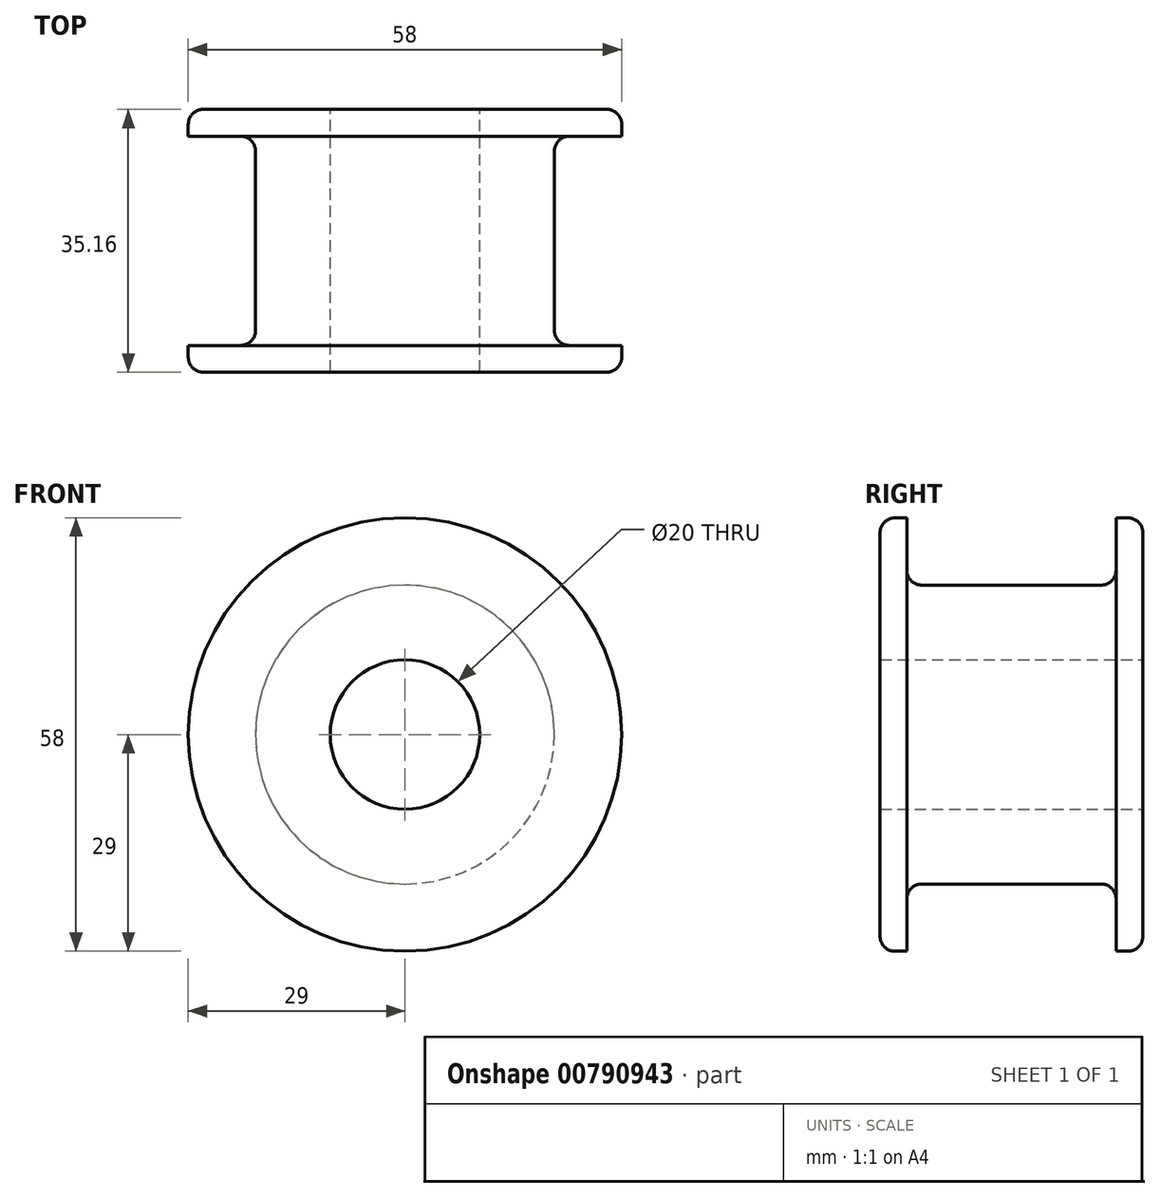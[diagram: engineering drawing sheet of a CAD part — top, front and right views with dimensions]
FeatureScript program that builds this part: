
annotation { "Feature Type Name" : "Feature", "Feature Type Description" : "" }
export const myFeature = defineFeature(function(context is Context, id is Id, definition is map)
    precondition{}
    {
        {
            var Q0;
            Q0=qCreatedBy(makeId("Top.planeOp"),FACE);
            var sketch = newSketch(context, id + "F0", { "sketchPlane" : qUnion([Q0])});
            skLineSegment(sketch, "E0", {"start": v(-29, -14) * mm, "end": v(-29, -17.6) * mm});
            skLineSegment(sketch, "E1", {"start": v(-29, -14) * mm, "end": v(-20, -14) * mm});
            skLineSegment(sketch, "E2", {"start": v(-20, -14) * mm, "end": v(-20, 0) * mm});
            skLineSegment(sketch, "E3", {"start": v(-20, 0) * mm, "end": v(0, 0) * mm});
            skLineSegment(sketch, "E4", {"start": v(0, 0) * mm, "end": v(0, -17.5) * mm});
            skLineSegment(sketch, "E5", {"start": v(-29, -17.6) * mm, "end": v(0, -17.5) * mm});
            skSolve(sketch);
        }
        {
            var Q0;
            Q0 = qSketchRegion(id + "F0", true);
            var Q1;
            Q1=sQuery(id+"F0.wireOp",EDGE,"E4");
            revolve(context, id + "F1", {"surfaceOperationType" : NewSurfaceOperationType.NEW, "entities" : qUnion([Q0]), "axis" : qUnion([Q1]), "revolveType" : RevolveType.FULL});
        }
        {
            var Q0;
            Q0=makeQuery(id+"F1.opRevolve","SWEPT_BODY",BODY,{"disambiguationData":[OSD([sQuery(id+"F0.wireOp",EDGE,"E0"),sQuery(id+"F0.wireOp",EDGE,"E1"),sQuery(id+"F0.wireOp",EDGE,"E2"),sQuery(id+"F0.wireOp",EDGE,"E3"),sQuery(id+"F0.wireOp",EDGE,"E4"),sQuery(id+"F0.wireOp",EDGE,"E5")])]});
            var Q1;
            Q1=qCreatedBy(makeId("Front.planeOp"),FACE);
            mirror(context, id + "F2", {"operationType" : NewBodyOperationType.ADD, "entities" : qUnion([Q0]), "mirrorPlane" : qUnion([Q1])});
        }
        {
            var Q0;
            Q0=makeQuery(id+"F2.opPattern","COPY",EDGE,{"derivedFrom":makeQuery(id+"F1.opRevolve","SWEPT_EDGE",EDGE,{"disambiguationData":[OSD([sQuery(id+"F0.wireOp",EDGE,"E1"),sQuery(id+"F0.wireOp",EDGE,"E2")])]}),"instanceName":"1"});
            fillet(context, id + "F3", {"entities" : qUnion([Q0]), "radius" : 2 * mm, "tangentPropagation" : true, "allowEdgeOverflow" : false});
        }
        {
            var Q0;
            Q0=makeQuery(id+"F1.opRevolve","SWEPT_EDGE",EDGE,{"disambiguationData":[OSD([sQuery(id+"F0.wireOp",EDGE,"E1"),sQuery(id+"F0.wireOp",EDGE,"E2")])]});
            var Q1;
            Q1=makeQuery(id+"F1.opRevolve","SWEPT_EDGE",EDGE,{"disambiguationData":[OSD([sQuery(id+"F0.wireOp",EDGE,"E0"),sQuery(id+"F0.wireOp",EDGE,"E5")])]});
            var Q2;
            Q2=makeQuery(id+"F2.opPattern","COPY",EDGE,{"derivedFrom":makeQuery(id+"F1.opRevolve","SWEPT_EDGE",EDGE,{"disambiguationData":[OSD([sQuery(id+"F0.wireOp",EDGE,"E0"),sQuery(id+"F0.wireOp",EDGE,"E5")])]}),"instanceName":"1"});
            fillet(context, id + "F4", {"entities" : qUnion([Q0, Q1, Q2]), "radius" : 2 * mm, "tangentPropagation" : true, "allowEdgeOverflow" : false});
        }
        {
            var Q0;
            Q0=qCreatedBy(makeId("Front.planeOp"),FACE);
            var sketch = newSketch(context, id + "F5", { "sketchPlane" : qUnion([Q0])});
            skCircle(sketch, "E6", {"center": v(0, 0) * mm, "radius": 10 * mm});
            skSolve(sketch);
        }
        {
            var Q0;
            Q0 = qSketchRegion(id + "F5", true);
            extrude(context, id + "F6", {"entities" : qUnion([Q0]), "operationType" : NewBodyOperationType.REMOVE, "endBound" : BoundingType.SYMMETRIC, "depth" : 40 * mm, "offsetDistance" : 25 * mm});
        }
    });
